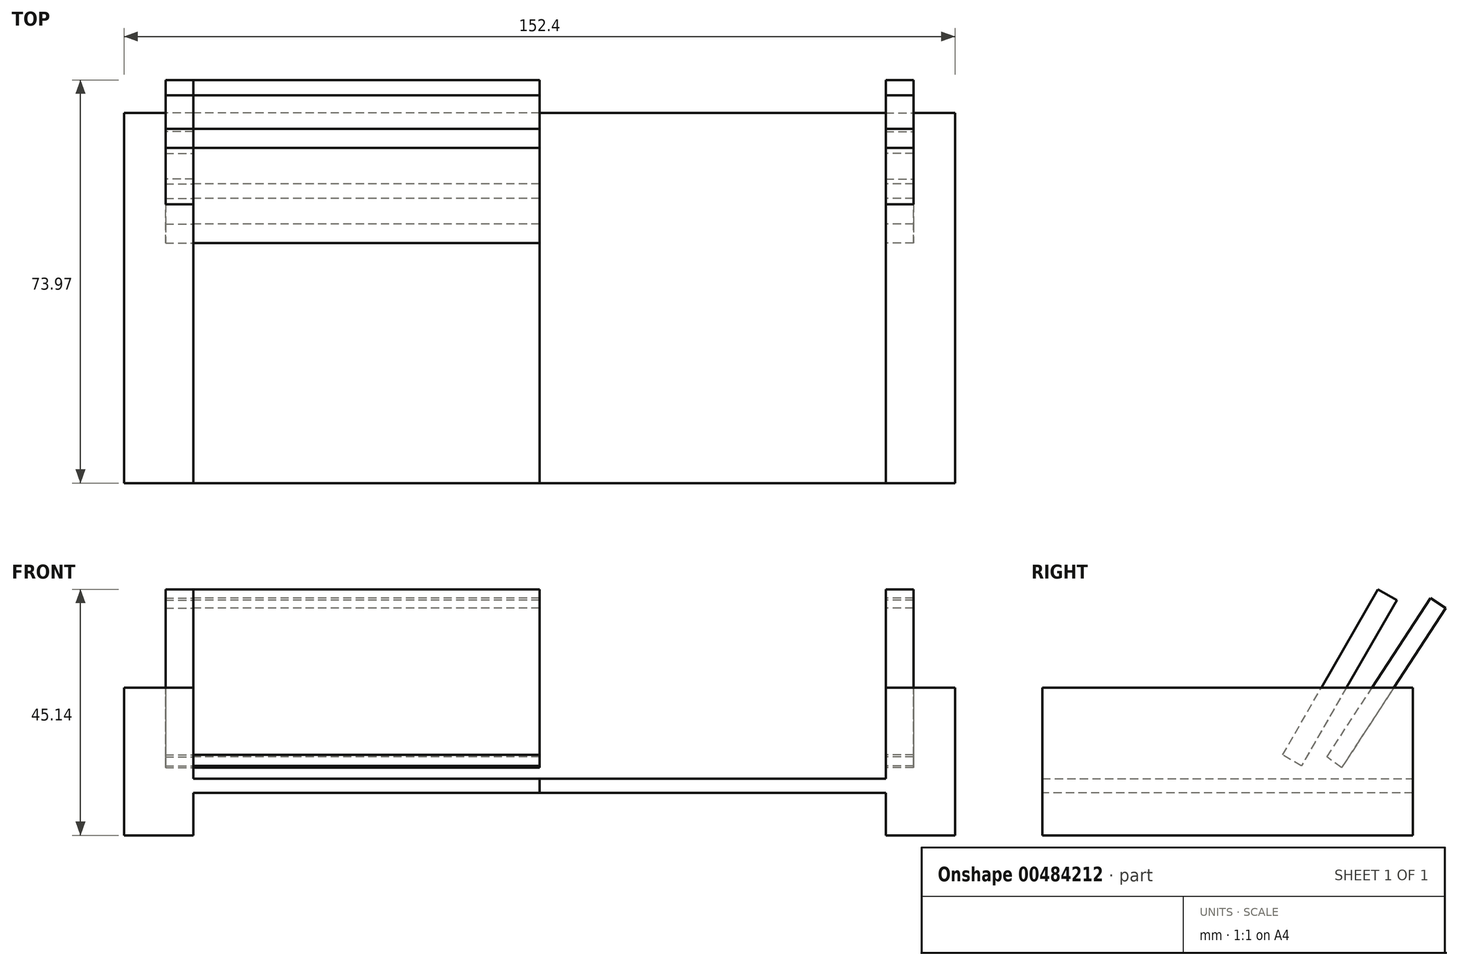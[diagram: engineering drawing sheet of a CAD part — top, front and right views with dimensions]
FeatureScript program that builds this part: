
annotation { "Feature Type Name" : "Feature", "Feature Type Description" : "" }
export const myFeature = defineFeature(function(context is Context, id is Id, definition is map)
    precondition{}
    {
        {
            var Q0;
            Q0=qCreatedBy(makeId("Right.planeOp"),FACE);
            var sketch = newSketch(context, id + "F0", { "sketchPlane" : qUnion([Q0])});
            skLineSegment(sketch, "E0", {"start": v(0, 0) * mm, "end": v(0, -27.1) * mm});
            skLineSegment(sketch, "E1", {"start": v(0, -27.1) * mm, "end": v(67.95, -27.1) * mm});
            skLineSegment(sketch, "E2", {"start": v(67.95, -27.1) * mm, "end": v(67.95, 0) * mm});
            skLineSegment(sketch, "E3", {"start": v(67.95, 0) * mm, "end": v(0, 0) * mm});
            skLineSegment(sketch, "E4", {"start": v(67.95, -16.73) * mm, "end": v(0, -16.73) * mm});
            skLineSegment(sketch, "E5", {"start": v(0, -19.32) * mm, "end": v(67.95, -19.32) * mm});
            skSolve(sketch);
        }
        {
            var Q0;
            {var subQ0=sQuery(id+"F0.wireOp",EDGE,"E3");Q0=makeQuery(id+"F0.imprint","IMPRINT",FACE,{"disambiguationData":[TD([[makeQuery(id+"F0.imprint","IMPRINT",EDGE,{"derivedFrom":subQ0}),1.0]])]});}
            var Q1;
            {var subQ0=sQuery(id+"F0.wireOp",EDGE,"E4");Q1=makeQuery(id+"F0.imprint","IMPRINT",FACE,{"disambiguationData":[TD([[makeQuery(id+"F0.imprint","IMPRINT",EDGE,{"derivedFrom":subQ0}),1.0]])]});}
            var Q2;
            {var subQ0=sQuery(id+"F0.wireOp",EDGE,"E1");Q2=makeQuery(id+"F0.imprint","IMPRINT",FACE,{"disambiguationData":[TD([[makeQuery(id+"F0.imprint","IMPRINT",EDGE,{"derivedFrom":subQ0}),1.0]])]});}
            extrude(context, id + "F1", {"entities" : qUnion([Q0, Q1, Q2]), "depth" : 12.7 * mm});
        }
        {
            var Q0;
            {var subQ0=sQuery(id+"F0.wireOp",EDGE,"E4");Q0=makeQuery(id+"F0.imprint","IMPRINT",FACE,{"disambiguationData":[TD([[makeQuery(id+"F0.imprint","IMPRINT",EDGE,{"derivedFrom":subQ0}),1.0]])]});}
            extrude(context, id + "F2", {"entities" : qUnion([Q0]), "operationType" : NewBodyOperationType.ADD, "depth" : 76.2 * mm});
        }
        {
            var Q0;
            {var subQ0=sQuery(id+"F0.wireOp",EDGE,"E0");var subQ1=sQuery(id+"F0.wireOp",EDGE,"E2");var subQ2=sQuery(id+"F0.wireOp",EDGE,"E3");Q0=makeQuery(id+"F2.boolean.opBoolean","SPLIT",FACE,{"disambiguationData":[TD([makeQuery(id+"F1.opExtrude","SWEPT_FACE",FACE,{"disambiguationData":[OSD([subQ2])]})])],"derivedFrom":makeQuery(id+"F1.opExtrude","CAP_FACE",FACE,{"disambiguationData":[OSD([subQ0,sQuery(id+"F0.wireOp",EDGE,"E1"),subQ1,subQ2])],"isStart":false})});}
            var sketch = newSketch(context, id + "F3", { "sketchPlane" : qUnion([Q0])});
            skLineSegment(sketch, "E6", {"start": v(44.07, -12.35) * mm, "end": v(61.54, 18.04) * mm});
            skLineSegment(sketch, "E7", {"start": v(61.54, 18.04) * mm, "end": v(65, 16.05) * mm});
            skLineSegment(sketch, "E8", {"start": v(65, 16.05) * mm, "end": v(47.53, -14.36) * mm});
            skLineSegment(sketch, "E9", {"start": v(47.53, -14.36) * mm, "end": v(44.07, -12.35) * mm});
            skLineSegment(sketch, "E10", {"start": v(52.22, -12.69) * mm, "end": v(71.17, 16.4) * mm});
            skLineSegment(sketch, "E11", {"start": v(71.17, 16.4) * mm, "end": v(73.97, 14.58) * mm});
            skLineSegment(sketch, "E12", {"start": v(73.97, 14.58) * mm, "end": v(54.9, -14.7) * mm});
            skLineSegment(sketch, "E13", {"start": v(54.9, -14.7) * mm, "end": v(52.22, -12.69) * mm});
            skSolve(sketch);
        }
        {
            var Q0;
            {var subQ0=sQuery(id+"F3.wireOp",EDGE,"E11");Q0=makeQuery(id+"F3.imprint","IMPRINT",FACE,{"disambiguationData":[TD([[makeQuery(id+"F3.imprint","IMPRINT",EDGE,{"derivedFrom":subQ0}),-1.0]])]});}
            var Q1;
            {var subQ0=sQuery(id+"F3.wireOp",EDGE,"E7");Q1=makeQuery(id+"F3.imprint","IMPRINT",FACE,{"disambiguationData":[TD([[makeQuery(id+"F3.imprint","IMPRINT",EDGE,{"derivedFrom":subQ0}),-1.0]])]});}
            var Q2;
            {var subQ0=sQuery(id+"F3.wireOp",EDGE,"E9");Q2=makeQuery(id+"F3.imprint","IMPRINT",FACE,{"disambiguationData":[TD([[makeQuery(id+"F3.imprint","IMPRINT",EDGE,{"derivedFrom":subQ0}),-1.0]])]});}
            var Q3;
            {var subQ0=sQuery(id+"F3.wireOp",EDGE,"E13");Q3=makeQuery(id+"F3.imprint","IMPRINT",FACE,{"disambiguationData":[TD([[makeQuery(id+"F3.imprint","IMPRINT",EDGE,{"derivedFrom":subQ0}),-1.0]])]});}
            extrude(context, id + "F4", {"entities" : qUnion([Q0, Q1, Q2, Q3]), "operationType" : NewBodyOperationType.REMOVE, "oppositeDirection" : true, "depth" : 5.08 * mm});
        }
        {
            var Q0;
            Q0 = qSketchRegion(id + "F3", true);
            extrude(context, id + "F5", {"entities" : qUnion([Q0]), "depth" : 63.5 * mm});
        }
        {
            var Q0;
            Q0 = qSketchRegion(id + "F3", true);
            extrude(context, id + "F6", {"entities" : qUnion([Q0]), "oppositeDirection" : true, "depth" : 5.08 * mm});
        }
        {
            var Q0;
            Q0=makeQuery(id+"F6.opExtrude","SWEPT_BODY",BODY,{"disambiguationData":[OSD([sQuery(id+"F3.wireOp",EDGE,"E6"),sQuery(id+"F3.wireOp",EDGE,"E7"),sQuery(id+"F3.wireOp",EDGE,"E8"),sQuery(id+"F3.wireOp",EDGE,"E9")])]});
            var Q1;
            Q1=makeQuery(id+"F6.opExtrude","SWEPT_BODY",BODY,{"disambiguationData":[OSD([sQuery(id+"F3.wireOp",EDGE,"E10"),sQuery(id+"F3.wireOp",EDGE,"E11"),sQuery(id+"F3.wireOp",EDGE,"E12"),sQuery(id+"F3.wireOp",EDGE,"E13")])]});
            var Q2;
            Q2=makeQuery(id+"F1.opExtrude","SWEPT_BODY",BODY,{"disambiguationData":[OSD([sQuery(id+"F0.wireOp",EDGE,"E0"),sQuery(id+"F0.wireOp",EDGE,"E1"),sQuery(id+"F0.wireOp",EDGE,"E2"),sQuery(id+"F0.wireOp",EDGE,"E3")])]});
            var Q3;
            Q3=makeQuery(id+"F2.opExtrude","CAP_FACE",FACE,{"disambiguationData":[OSD([sQuery(id+"F0.wireOp",EDGE,"E0"),sQuery(id+"F0.wireOp",EDGE,"E2"),sQuery(id+"F0.wireOp",EDGE,"E4"),sQuery(id+"F0.wireOp",EDGE,"E5")])],"isStart":false});
            mirror(context, id + "F7", {"entities" : qUnion([Q0, Q1, Q2]), "mirrorPlane" : qUnion([Q3])});
        }
    });
